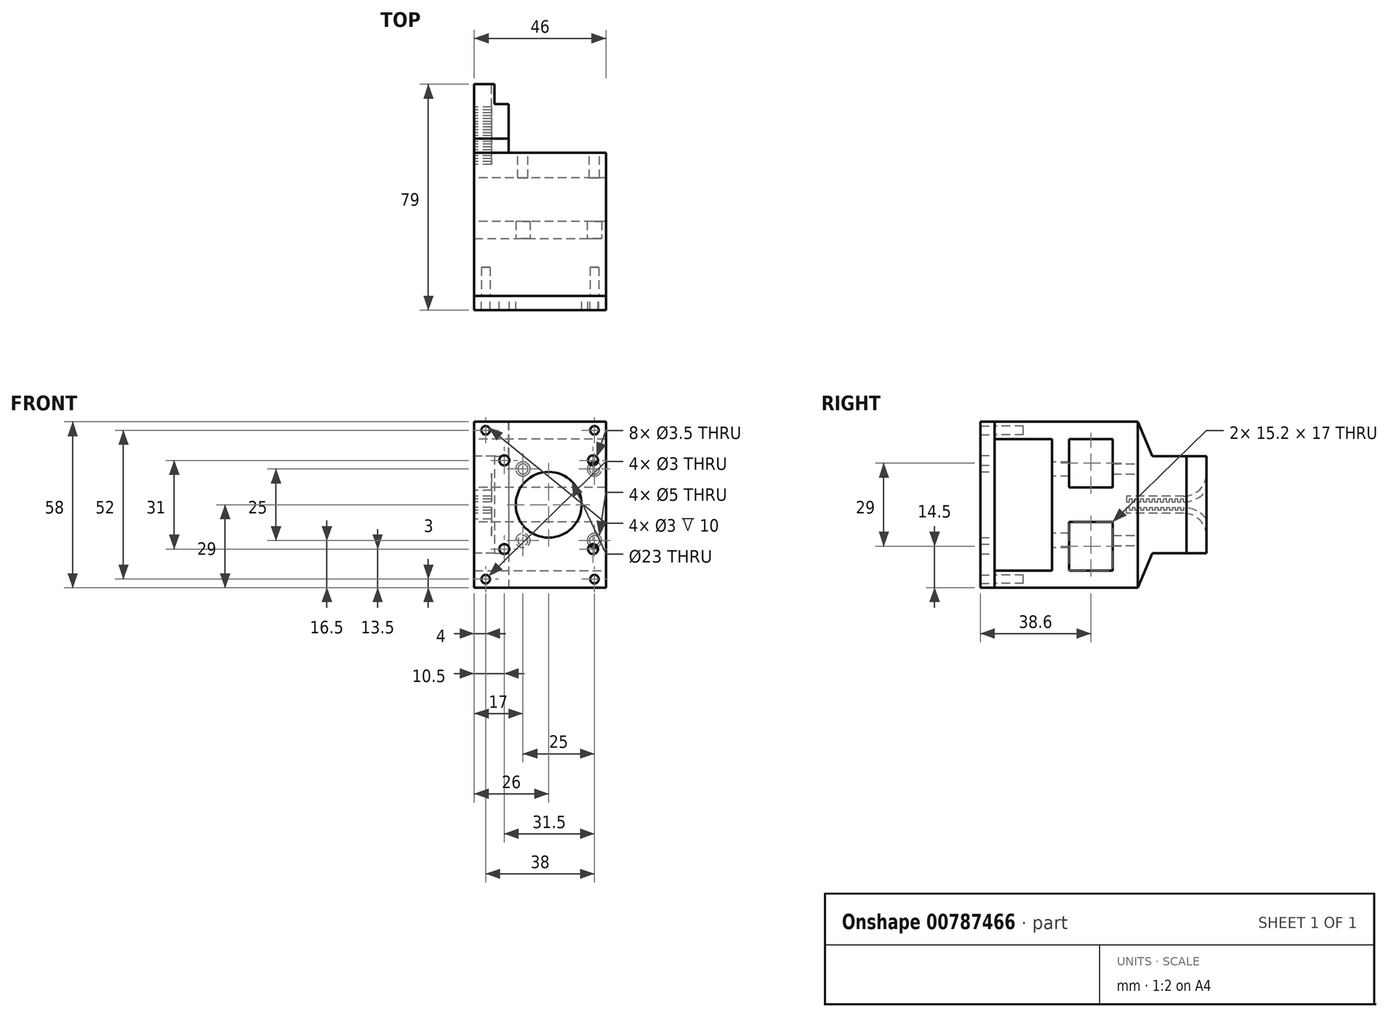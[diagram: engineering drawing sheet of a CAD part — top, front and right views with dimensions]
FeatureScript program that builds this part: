
annotation { "Feature Type Name" : "Feature", "Feature Type Description" : "" }
export const myFeature = defineFeature(function(context is Context, id is Id, definition is map)
    precondition{}
    {
        {
            var Q0;
            Q0=qCreatedBy(makeId("Front.planeOp"),FACE);
            var sketch = newSketch(context, id + "F0", { "sketchPlane" : qUnion([Q0])});
            skLineSegment(sketch, "E0.bottom", {"start": v(0, 0) * mm, "end": v(46, 0) * mm});
            skLineSegment(sketch, "E0.top", {"start": v(0, 58) * mm, "end": v(46, 58) * mm});
            skLineSegment(sketch, "E0.left", {"start": v(0, 0) * mm, "end": v(0, 58) * mm});
            skLineSegment(sketch, "E0.right", {"start": v(46, 0) * mm, "end": v(46, 58) * mm});
            skCircle(sketch, "E1", {"center": v(17, 16.5) * mm, "radius": 1.75 * mm});
            skCircle(sketch, "E2", {"center": v(42, 16.5) * mm, "radius": 1.75 * mm});
            skCircle(sketch, "E3", {"center": v(42, 41.5) * mm, "radius": 1.75 * mm});
            skCircle(sketch, "E4", {"center": v(17, 41.5) * mm, "radius": 1.75 * mm});
            skLineSegment(sketch, "E5", {"start": v(-7.47, 16.5) * mm, "end": v(45.4, 16.5) * mm, "construction": true});
            skLineSegment(sketch, "E6", {"start": v(-6.97, 41.5) * mm, "end": v(44.16, 41.5) * mm, "construction": true});
            skLineSegment(sketch, "E7", {"start": v(17, -1.28) * mm, "end": v(17, 38.84) * mm, "construction": true});
            skLineSegment(sketch, "E8", {"start": v(42, -1.84) * mm, "end": v(42, 37.95) * mm, "construction": true});
            skLineSegment(sketch, "E9", {"start": v(42, 37.95) * mm, "end": v(41.66, 37.95) * mm, "construction": true});
            skSolve(sketch);
        }
        {
            var Q0;
            Q0=makeQuery(id+"F0.imprint","IMPRINT",FACE,{"disambiguationData":[TD([[makeQuery(id+"F0.imprint","IMPRINT",EDGE,{"derivedFrom":sQuery(id+"F0.wireOp",EDGE,"E0.bottom")}),1.0]])]});
            extrude(context, id + "F1", {"entities" : qUnion([Q0]), "depth" : 30 * mm, "offsetDistance" : 25 * mm});
        }
        {
            var Q0;
            Q0=makeQuery(id+"Fh8Oho9HevaeckM_1.boolean.opBoolean","MERGE",FACE,{"derivedFrom":[makeQuery(id+"F5.boolean.opBoolean","MERGE",FACE,{"derivedFrom":[makeQuery(id+"F1.opExtrude","SWEPT_FACE",FACE,{"disambiguationData":[OSD([sQuery(id+"F0.wireOp",EDGE,"E0.left")])]}),makeQuery(id+"F5.opExtrude","SWEPT_FACE",FACE,{"disambiguationData":[OSD([sQuery(id+"F4.wireOp",EDGE,"E16.right")])]})]}),makeQuery(id+"Fh8Oho9HevaeckM_1.opExtrude","SWEPT_FACE",FACE,{"disambiguationData":[OSD([sQuery(id+"FOvHqaYxA9nbsMf_1.wireOp",EDGE,"oteaciAY-sE7d-qbvy-cTgZ-kNNArxGtZx8z.left")])]})]});
            var sketch = newSketch(context, id + "F2", { "sketchPlane" : qUnion([Q0])});
            skLineSegment(sketch, "E10.bottom", {"start": v(8.8, 6) * mm, "end": v(24, 6) * mm});
            skLineSegment(sketch, "E10.top", {"start": v(8.8, 23) * mm, "end": v(24, 23) * mm});
            skLineSegment(sketch, "E10.left", {"start": v(8.8, 6) * mm, "end": v(8.8, 23) * mm});
            skLineSegment(sketch, "E10.right", {"start": v(24, 6) * mm, "end": v(24, 23) * mm});
            skPoint(sketch, "E10.middle", {"position": v(16.4, 14.5) * mm});
            skLineSegment(sketch, "E11", {"start": v(30, 29) * mm, "end": v(0, 29) * mm, "construction": true});
            skLineSegment(sketch, "E12.MirrorCS", {"start": v(8.8, 35) * mm, "end": v(24, 35) * mm});
            skLineSegment(sketch, "E13.MirrorCS", {"start": v(24, 52) * mm, "end": v(24, 35) * mm});
            skLineSegment(sketch, "E14.MirrorCS", {"start": v(8.8, 52) * mm, "end": v(24, 52) * mm});
            skLineSegment(sketch, "E15.MirrorCS", {"start": v(8.8, 52) * mm, "end": v(8.8, 35) * mm});
            skSolve(sketch);
        }
        {
            var Q0;
            Q0=qSketchRegion(id+"F2",true);
            extrude(context, id + "F3", {"entities" : qUnion([Q0]), "operationType" : NewBodyOperationType.REMOVE, "endBound" : BoundingType.THROUGH_ALL, "oppositeDirection" : true, "depth" : 25 * mm, "offsetDistance" : 25 * mm});
        }
        {
            var Q0;
            {var subQ0=sQuery(id+"F0.wireOp",EDGE,"E1");var subQ1=sQuery(id+"F0.wireOp",EDGE,"E0.right");var subQ2=sQuery(id+"F0.wireOp",EDGE,"E0.left");var subQ3=sQuery(id+"F0.wireOp",EDGE,"E0.top");var subQ4=sQuery(id+"F0.wireOp",EDGE,"E2");var subQ5=sQuery(id+"F0.wireOp",EDGE,"E3");var subQ6=sQuery(id+"F0.wireOp",EDGE,"E4");Q0=makeQuery(id+"FCBNdEiGlgR24Ja_1.boolean.opBoolean","SPLIT",FACE,{"disambiguationData":[TD([makeQuery(id+"F1.opExtrude","SWEPT_FACE",FACE,{"disambiguationData":[OSD([subQ3])]})])],"derivedFrom":makeQuery(id+"F1.opExtrude","CAP_FACE",FACE,{"disambiguationData":[OSD([sQuery(id+"F0.wireOp",EDGE,"E0.bottom"),subQ3,subQ2,subQ1,subQ0,subQ4,subQ5,subQ6])],"isStart":false})});}
            var sketch = newSketch(context, id + "F4", { "sketchPlane" : qUnion([Q0])});
            skLineSegment(sketch, "E16.bottom", {"start": v(46, 58) * mm, "end": v(0, 58) * mm});
            skLineSegment(sketch, "E16.top", {"start": v(46, 52) * mm, "end": v(0, 52) * mm});
            skLineSegment(sketch, "E16.left", {"start": v(46, 52) * mm, "end": v(46, 58) * mm});
            skLineSegment(sketch, "E16.right", {"start": v(0, 52) * mm, "end": v(0, 58) * mm});
            skLineSegment(sketch, "E17.bottom", {"start": v(0, 0) * mm, "end": v(46, 0) * mm});
            skLineSegment(sketch, "E17.top", {"start": v(0, 6) * mm, "end": v(46, 6) * mm});
            skLineSegment(sketch, "E17.left", {"start": v(0, 0) * mm, "end": v(0, 6) * mm});
            skLineSegment(sketch, "E17.right", {"start": v(46, 0) * mm, "end": v(46, 6) * mm});
            skSolve(sketch);
        }
        {
            var Q0;
            Q0 = qSketchRegion(id + "F4", true);
            extrude(context, id + "F5", {"entities" : qUnion([Q0]), "operationType" : NewBodyOperationType.ADD, "depth" : 20 * mm, "offsetDistance" : 25 * mm});
        }
        {
            var Q0;
            Q0=makeQuery(id+"F5.opExtrude","CAP_FACE",FACE,{"disambiguationData":[OSD([sQuery(id+"F4.wireOp",EDGE,"E16.bottom"),sQuery(id+"F4.wireOp",EDGE,"E16.top"),sQuery(id+"F4.wireOp",EDGE,"E16.left"),sQuery(id+"F4.wireOp",EDGE,"E16.right")])],"isStart":false});
            var sketch = newSketch(context, id + "F6", { "sketchPlane" : qUnion([Q0])});
            skLineSegment(sketch, "E18", {"start": v(26, 81.43) * mm, "end": v(26, 7.23) * mm, "construction": true});
            skPoint(sketch, "E18.startSnap0", {"position": v(26, 65.8) * mm});
            skLineSegment(sketch, "E19", {"start": v(-30.8, 29) * mm, "end": v(63.7, 29) * mm, "construction": true});
            skCircle(sketch, "E20", {"center": v(26, 29) * mm, "radius": 11.5 * mm});
            skCircle(sketch, "E21", {"center": v(10.5, 44.5) * mm, "radius": 1.75 * mm});
            skCircle(sketch, "E22.MirrorC", {"center": v(41.5, 44.5) * mm, "radius": 1.75 * mm});
            skCircle(sketch, "E23.MirrorC", {"center": v(10.5, 13.5) * mm, "radius": 1.75 * mm});
            skCircle(sketch, "E24.MirrorC", {"center": v(41.5, 13.5) * mm, "radius": 1.75 * mm});
            skLineSegment(sketch, "E25.bottom", {"start": v(46, 58) * mm, "end": v(0, 58) * mm});
            skLineSegment(sketch, "E25.top", {"start": v(46, 52) * mm, "end": v(0, 52) * mm});
            skLineSegment(sketch, "E25.left", {"start": v(46, 58) * mm, "end": v(46, 52) * mm});
            skLineSegment(sketch, "E25.right", {"start": v(0, 58) * mm, "end": v(0, 52) * mm});
            skLineSegment(sketch, "E26.bottom", {"start": v(0, 0) * mm, "end": v(46, 0) * mm});
            skLineSegment(sketch, "E26.top", {"start": v(0, 4.54) * mm, "end": v(46, 4.54) * mm});
            skLineSegment(sketch, "E26.left", {"start": v(0, 0) * mm, "end": v(0, 4.54) * mm});
            skLineSegment(sketch, "E26.right", {"start": v(46, 0) * mm, "end": v(46, 4.54) * mm});
            skLineSegment(sketch, "E27", {"start": v(46, 4.54) * mm, "end": v(46, 52) * mm});
            skLineSegment(sketch, "E28", {"start": v(0, 4.54) * mm, "end": v(0, 52) * mm});
            skSolve(sketch);
        }
        {
            var Q0;
            Q0 = qSketchRegion(id + "F6", true);
            extrude(context, id + "F7", {"entities" : qUnion([Q0]), "depth" : 5 * mm, "offsetDistance" : 25 * mm});
        }
        {
            var Q0;
            Q0=makeQuery(id+"F1.opExtrude","CAP_FACE",FACE,{"disambiguationData":[OSD([sQuery(id+"F0.wireOp",EDGE,"E0.bottom"),sQuery(id+"F0.wireOp",EDGE,"E0.top"),sQuery(id+"F0.wireOp",EDGE,"E0.left"),sQuery(id+"F0.wireOp",EDGE,"E0.right"),sQuery(id+"F0.wireOp",EDGE,"E1"),sQuery(id+"F0.wireOp",EDGE,"E2"),sQuery(id+"F0.wireOp",EDGE,"E3"),sQuery(id+"F0.wireOp",EDGE,"E4")])],"isStart":false});
            var sketch = newSketch(context, id + "F8", { "sketchPlane" : qUnion([Q0])});
            skCircle(sketch, "E29", {"center": v(17, 41.5) * mm, "radius": 2.5 * mm});
            skCircle(sketch, "E30", {"center": v(17, 16.5) * mm, "radius": 2.5 * mm});
            skCircle(sketch, "E31", {"center": v(42, 41.5) * mm, "radius": 2.5 * mm});
            skCircle(sketch, "E32", {"center": v(42, 16.5) * mm, "radius": 2.5 * mm});
            skSolve(sketch);
        }
        {
            var Q0;
            Q0 = qSketchRegion(id + "F8", true);
            extrude(context, id + "F9", {"entities" : qUnion([Q0]), "operationType" : NewBodyOperationType.REMOVE, "oppositeDirection" : true, "depth" : 10 * mm, "offsetDistance" : 25 * mm});
        }
        {
            var Q0;
            Q0=makeQuery(id+"F6.imprint","IMPRINT",FACE,{"disambiguationData":[TD([[makeQuery(id+"F6.imprint","IMPRINT",EDGE,{"derivedFrom":sQuery(id+"F6.wireOp",EDGE,"E26.bottom")}),1.0]])]});
            var sketch = newSketch(context, id + "F10", { "sketchPlane" : qUnion([Q0])});
            skLineSegment(sketch, "E33", {"start": v(41.02, 3) * mm, "end": v(0, 3) * mm, "construction": true});
            skCircle(sketch, "E34", {"center": v(42, 3) * mm, "radius": 1.5 * mm});
            skCircle(sketch, "E35", {"center": v(4, 3) * mm, "radius": 1.5 * mm});
            skLineSegment(sketch, "E36", {"start": v(46, 55) * mm, "end": v(0, 55) * mm, "construction": true});
            skCircle(sketch, "E37", {"center": v(42, 55) * mm, "radius": 1.5 * mm});
            skCircle(sketch, "E38", {"center": v(4, 55) * mm, "radius": 1.5 * mm});
            skSolve(sketch);
        }
        {
            var Q0;
            Q0 = qSketchRegion(id + "F10", true);
            extrude(context, id + "F11", {"entities" : qUnion([Q0]), "operationType" : NewBodyOperationType.REMOVE, "oppositeDirection" : true, "depth" : 10 * mm, "offsetDistance" : 25 * mm});
        }
        {
            var Q0;
            Q0 = qSketchRegion(id + "F10", true);
            extrude(context, id + "F12", {"entities" : qUnion([Q0]), "operationType" : NewBodyOperationType.REMOVE, "endBound" : BoundingType.THROUGH_ALL, "depth" : 25 * mm, "offsetDistance" : 25 * mm});
        }
        {
            var Q0;
            Q0=makeQuery(id+"F1.opExtrude","CAP_FACE",FACE,{"disambiguationData":[OSD([sQuery(id+"F0.wireOp",EDGE,"E0.bottom"),sQuery(id+"F0.wireOp",EDGE,"E0.top"),sQuery(id+"F0.wireOp",EDGE,"E0.left"),sQuery(id+"F0.wireOp",EDGE,"E0.right"),sQuery(id+"F0.wireOp",EDGE,"E1"),sQuery(id+"F0.wireOp",EDGE,"E2"),sQuery(id+"F0.wireOp",EDGE,"E3"),sQuery(id+"F0.wireOp",EDGE,"E4")])],"isStart":true});
            var sketch = newSketch(context, id + "F13", { "sketchPlane" : qUnion([Q0])});
            skLineSegment(sketch, "E39.bottom", {"start": v(0, 58) * mm, "end": v(-12, 58) * mm});
            skLineSegment(sketch, "E39.top", {"start": v(0, 0) * mm, "end": v(-12, 0) * mm});
            skLineSegment(sketch, "E39.left", {"start": v(0, 58) * mm, "end": v(0, 0) * mm});
            skLineSegment(sketch, "E39.right", {"start": v(-12, 58) * mm, "end": v(-12, 0) * mm});
            skSolve(sketch);
        }
        {
            var Q0;
            Q0=makeQuery(id+"F13.imprint","IMPRINT",FACE,{"disambiguationData":[TD([[makeQuery(id+"F13.imprint","IMPRINT",EDGE,{"derivedFrom":sQuery(id+"F13.wireOp",EDGE,"E39.bottom")}),1.0]])]});
            extrude(context, id + "F14", {"entities" : qUnion([Q0]), "operationType" : NewBodyOperationType.ADD, "depth" : 24 * mm, "offsetDistance" : 25 * mm});
        }
        {
            var Q0;
            Q0=makeQuery(id+"F14.boolean.opBoolean","MERGE",FACE,{"derivedFrom":[makeQuery(id+"F5.boolean.opBoolean","MERGE",FACE,{"derivedFrom":[makeQuery(id+"F1.opExtrude","SWEPT_FACE",FACE,{"disambiguationData":[OSD([sQuery(id+"F0.wireOp",EDGE,"E0.left")])]}),makeQuery(id+"F5.opExtrude","SWEPT_FACE",FACE,{"disambiguationData":[OSD([sQuery(id+"F4.wireOp",EDGE,"E16.right")])]}),makeQuery(id+"F5.opExtrude","SWEPT_FACE",FACE,{"disambiguationData":[OSD([sQuery(id+"F4.wireOp",EDGE,"E17.left")])]})]}),makeQuery(id+"F14.opExtrude","SWEPT_FACE",FACE,{"disambiguationData":[OSD([sQuery(id+"F13.wireOp",EDGE,"E39.left")])]})]});
            var sketch = newSketch(context, id + "F15", { "sketchPlane" : qUnion([Q0])});
            skLineSegment(sketch, "E40", {"start": v(-24, 29) * mm, "end": v(30, 29) * mm, "construction": true});
            skLineSegment(sketch, "E41", {"start": v(30, 29) * mm, "end": v(29.17, 29.8) * mm, "construction": true});
            skArc(sketch, "E42", {"start": v(-24, 40) * mm, "mid": v(-21.66, 34.34) * mm, "end": v(-16, 32) * mm});
            skLineSegment(sketch, "E43", {"start": v(-16, 32) * mm, "end": v(4, 32) * mm});
            skLineSegment(sketch, "E44", {"start": v(4, 32) * mm, "end": v(4, 30) * mm});
            skLineSegment(sketch, "E45", {"start": v(4, 30) * mm, "end": v(3, 30) * mm});
            skArc(sketch, "E46", {"start": v(-24, 34) * mm, "mid": v(-20.47, 31.06) * mm, "end": v(-16, 30) * mm});
            skPoint(sketch, "E47.start.orphan", {"position": v(0, 58) * mm});
            skLineSegment(sketch, "E48", {"start": v(-24, 34) * mm, "end": v(-24, 40) * mm});
            skLineSegment(sketch, "E49", {"start": v(-16, 40) * mm, "end": v(-16, 24.86) * mm, "construction": true});
            skLineSegment(sketch, "E50.top", {"start": v(2, 31) * mm, "end": v(3, 31) * mm});
            skLineSegment(sketch, "E50.left", {"start": v(2, 30) * mm, "end": v(2, 31) * mm});
            skLineSegment(sketch, "E50.right", {"start": v(3, 30) * mm, "end": v(3, 31) * mm});
            skLineSegment(sketch, "E51.1.0.0", {"start": v(0, 30) * mm, "end": v(0, 31) * mm});
            skLineSegment(sketch, "E51.1.0.1", {"start": v(0, 31) * mm, "end": v(1, 31) * mm});
            skLineSegment(sketch, "E51.1.0.2", {"start": v(2, 30) * mm, "end": v(1, 30) * mm});
            skLineSegment(sketch, "E51.1.0.3", {"start": v(1, 30) * mm, "end": v(1, 31) * mm});
            skLineSegment(sketch, "E51.2.0.0", {"start": v(-2, 30) * mm, "end": v(-2, 31) * mm});
            skLineSegment(sketch, "E51.2.0.1", {"start": v(-2, 31) * mm, "end": v(-1, 31) * mm});
            skLineSegment(sketch, "E51.2.0.2", {"start": v(0, 30) * mm, "end": v(-1, 30) * mm});
            skLineSegment(sketch, "E51.2.0.3", {"start": v(-1, 30) * mm, "end": v(-1, 31) * mm});
            skLineSegment(sketch, "E51.3.0.0", {"start": v(-4, 30) * mm, "end": v(-4, 31) * mm});
            skLineSegment(sketch, "E51.3.0.1", {"start": v(-4, 31) * mm, "end": v(-3, 31) * mm});
            skLineSegment(sketch, "E51.3.0.2", {"start": v(-2, 30) * mm, "end": v(-3, 30) * mm});
            skLineSegment(sketch, "E51.3.0.3", {"start": v(-3, 30) * mm, "end": v(-3, 31) * mm});
            skLineSegment(sketch, "E51.4.0.0", {"start": v(-6, 30) * mm, "end": v(-6, 31) * mm});
            skLineSegment(sketch, "E51.4.0.1", {"start": v(-6, 31) * mm, "end": v(-5, 31) * mm});
            skLineSegment(sketch, "E51.4.0.2", {"start": v(-4, 30) * mm, "end": v(-5, 30) * mm});
            skLineSegment(sketch, "E51.4.0.3", {"start": v(-5, 30) * mm, "end": v(-5, 31) * mm});
            skLineSegment(sketch, "E51.5.0.0", {"start": v(-8, 30) * mm, "end": v(-8, 31) * mm});
            skLineSegment(sketch, "E51.5.0.1", {"start": v(-8, 31) * mm, "end": v(-7, 31) * mm});
            skLineSegment(sketch, "E51.5.0.2", {"start": v(-6, 30) * mm, "end": v(-7, 30) * mm});
            skLineSegment(sketch, "E51.5.0.3", {"start": v(-7, 30) * mm, "end": v(-7, 31) * mm});
            skLineSegment(sketch, "E51.6.0.0", {"start": v(-10, 30) * mm, "end": v(-10, 31) * mm});
            skLineSegment(sketch, "E51.6.0.1", {"start": v(-10, 31) * mm, "end": v(-9, 31) * mm});
            skLineSegment(sketch, "E51.6.0.2", {"start": v(-8, 30) * mm, "end": v(-9, 30) * mm});
            skLineSegment(sketch, "E51.6.0.3", {"start": v(-9, 30) * mm, "end": v(-9, 31) * mm});
            skLineSegment(sketch, "E51.7.0.0", {"start": v(-12, 30) * mm, "end": v(-12, 31) * mm});
            skLineSegment(sketch, "E51.7.0.1", {"start": v(-12, 31) * mm, "end": v(-11, 31) * mm});
            skLineSegment(sketch, "E51.7.0.2", {"start": v(-10, 30) * mm, "end": v(-11, 30) * mm});
            skLineSegment(sketch, "E51.7.0.3", {"start": v(-11, 30) * mm, "end": v(-11, 31) * mm});
            skLineSegment(sketch, "E51.8.0.0", {"start": v(-14, 30) * mm, "end": v(-14, 31) * mm});
            skLineSegment(sketch, "E51.8.0.1", {"start": v(-14, 31) * mm, "end": v(-13, 31) * mm});
            skLineSegment(sketch, "E51.8.0.2", {"start": v(-12, 30) * mm, "end": v(-13, 30) * mm});
            skLineSegment(sketch, "E51.8.0.3", {"start": v(-13, 30) * mm, "end": v(-13, 31) * mm});
            skLineSegment(sketch, "E51.9.0.0", {"start": v(-16, 30) * mm, "end": v(-16, 31) * mm});
            skLineSegment(sketch, "E51.9.0.1", {"start": v(-16, 31) * mm, "end": v(-15, 31) * mm});
            skLineSegment(sketch, "E51.9.0.2", {"start": v(-14, 30) * mm, "end": v(-15, 30) * mm});
            skLineSegment(sketch, "E51.9.0.3", {"start": v(-15, 30) * mm, "end": v(-15, 31) * mm});
            skLineSegment(sketch, "E51.direction1", {"start": v(2, 30) * mm, "end": v(0, 30) * mm, "construction": true});
            skLineSegment(sketch, "E52.MirrorCS", {"start": v(-3, 28) * mm, "end": v(-3, 27) * mm});
            skLineSegment(sketch, "E53.MirrorCS", {"start": v(-11, 28) * mm, "end": v(-11, 27) * mm});
            skLineSegment(sketch, "E54.MirrorCS", {"start": v(-6, 27) * mm, "end": v(-5, 27) * mm});
            skLineSegment(sketch, "E55.MirrorCS", {"start": v(-14, 27) * mm, "end": v(-13, 27) * mm});
            skLineSegment(sketch, "E56.MirrorCS", {"start": v(-5, 28) * mm, "end": v(-5, 27) * mm});
            skLineSegment(sketch, "E57.MirrorCS", {"start": v(-13, 28) * mm, "end": v(-13, 27) * mm});
            skLineSegment(sketch, "E58.MirrorCS", {"start": v(0, 28) * mm, "end": v(0, 27) * mm});
            skLineSegment(sketch, "E59.MirrorCS", {"start": v(3, 28) * mm, "end": v(3, 27) * mm});
            skLineSegment(sketch, "E60.MirrorCS", {"start": v(2, 28) * mm, "end": v(2, 27) * mm});
            skLineSegment(sketch, "E61.MirrorCS", {"start": v(2, 27) * mm, "end": v(3, 27) * mm});
            skLineSegment(sketch, "E62.MirrorCS", {"start": v(4, 28) * mm, "end": v(3, 28) * mm});
            skLineSegment(sketch, "E63.MirrorCS", {"start": v(-10, 28) * mm, "end": v(-10, 27) * mm});
            skLineSegment(sketch, "E64.MirrorCS", {"start": v(2, 28) * mm, "end": v(0, 28) * mm, "construction": true});
            skLineSegment(sketch, "E65.MirrorCS", {"start": v(-2, 28) * mm, "end": v(-2, 27) * mm});
            skLineSegment(sketch, "E66.MirrorCS", {"start": v(2, 28) * mm, "end": v(1, 28) * mm});
            skLineSegment(sketch, "E67.MirrorCS", {"start": v(-8, 28) * mm, "end": v(-9, 28) * mm});
            skLineSegment(sketch, "E68.MirrorCS", {"start": v(0, 27) * mm, "end": v(1, 27) * mm});
            skLineSegment(sketch, "E69.MirrorCS", {"start": v(0, 28) * mm, "end": v(-1, 28) * mm});
            skLineSegment(sketch, "E70.MirrorCS", {"start": v(1, 28) * mm, "end": v(1, 27) * mm});
            skLineSegment(sketch, "E71.MirrorCS", {"start": v(-12, 28) * mm, "end": v(-12, 27) * mm});
            skLineSegment(sketch, "E72.MirrorCS", {"start": v(-8, 27) * mm, "end": v(-7, 27) * mm});
            skLineSegment(sketch, "E73.MirrorCS", {"start": v(-16, 27) * mm, "end": v(-15, 27) * mm});
            skLineSegment(sketch, "E74.MirrorCS", {"start": v(-4, 28) * mm, "end": v(-4, 27) * mm});
            skLineSegment(sketch, "E75.MirrorCS", {"start": v(-2, 28) * mm, "end": v(-3, 28) * mm});
            skLineSegment(sketch, "E76.MirrorCS", {"start": v(-10, 28) * mm, "end": v(-11, 28) * mm});
            skLineSegment(sketch, "E77.MirrorCS", {"start": v(-6, 28) * mm, "end": v(-6, 27) * mm});
            skLineSegment(sketch, "E78.MirrorCS", {"start": v(-14, 28) * mm, "end": v(-14, 27) * mm});
            skLineSegment(sketch, "E79.MirrorCS", {"start": v(-4, 28) * mm, "end": v(-5, 28) * mm});
            skLineSegment(sketch, "E80.MirrorCS", {"start": v(-12, 28) * mm, "end": v(-13, 28) * mm});
            skLineSegment(sketch, "E81.MirrorCS", {"start": v(-8, 28) * mm, "end": v(-8, 27) * mm});
            skLineSegment(sketch, "E82.MirrorCS", {"start": v(-16, 28) * mm, "end": v(-16, 27) * mm});
            skLineSegment(sketch, "E83.MirrorCS", {"start": v(-10, 27) * mm, "end": v(-9, 27) * mm});
            skLineSegment(sketch, "E84.MirrorCS", {"start": v(-2, 27) * mm, "end": v(-1, 27) * mm});
            skLineSegment(sketch, "E85.MirrorCS", {"start": v(-7, 28) * mm, "end": v(-7, 27) * mm});
            skLineSegment(sketch, "E86.MirrorCS", {"start": v(-9, 28) * mm, "end": v(-9, 27) * mm});
            skLineSegment(sketch, "E87.MirrorCS", {"start": v(-15, 28) * mm, "end": v(-15, 27) * mm});
            skLineSegment(sketch, "E88.MirrorCS", {"start": v(-1, 28) * mm, "end": v(-1, 27) * mm});
            skLineSegment(sketch, "E89.MirrorCS", {"start": v(-12, 27) * mm, "end": v(-11, 27) * mm});
            skLineSegment(sketch, "E90.MirrorCS", {"start": v(-6, 28) * mm, "end": v(-7, 28) * mm});
            skLineSegment(sketch, "E91.MirrorCS", {"start": v(-14, 28) * mm, "end": v(-15, 28) * mm});
            skLineSegment(sketch, "E92.MirrorCS", {"start": v(-4, 27) * mm, "end": v(-3, 27) * mm});
            skLineSegment(sketch, "E93.MirrorCS", {"start": v(-16, 18) * mm, "end": v(-16, 33.14) * mm, "construction": true});
            skLineSegment(sketch, "E94.MirrorCS", {"start": v(-24, 24) * mm, "end": v(-24, 18) * mm});
            skArc(sketch, "E95.MirrorCS", {"start": v(-24, 24) * mm, "mid": v(-20.47, 26.94) * mm, "end": v(-16, 28) * mm});
            skLineSegment(sketch, "E96.MirrorCS", {"start": v(4, 26) * mm, "end": v(4, 28) * mm});
            skLineSegment(sketch, "E97.MirrorCS", {"start": v(-16, 26) * mm, "end": v(4, 26) * mm});
            skArc(sketch, "E98.MirrorCS", {"start": v(-24, 18) * mm, "mid": v(-21.66, 23.66) * mm, "end": v(-16, 26) * mm});
            skSolve(sketch);
        }
        {
            var Q0;
            Q0 = qSketchRegion(id + "F15", true);
            extrude(context, id + "F16", {"entities" : qUnion([Q0]), "operationType" : NewBodyOperationType.REMOVE, "oppositeDirection" : true, "depth" : 6 * mm, "offsetDistance" : 25 * mm});
        }
        {
            var Q0;
            Q0=makeQuery(id+"F14.boolean.opBoolean","MERGE",FACE,{"derivedFrom":[makeQuery(id+"F5.boolean.opBoolean","MERGE",FACE,{"derivedFrom":[makeQuery(id+"F1.opExtrude","SWEPT_FACE",FACE,{"disambiguationData":[OSD([sQuery(id+"F0.wireOp",EDGE,"E0.left")])]}),makeQuery(id+"F5.opExtrude","SWEPT_FACE",FACE,{"disambiguationData":[OSD([sQuery(id+"F4.wireOp",EDGE,"E16.right")])]}),makeQuery(id+"F5.opExtrude","SWEPT_FACE",FACE,{"disambiguationData":[OSD([sQuery(id+"F4.wireOp",EDGE,"E17.left")])]})]}),makeQuery(id+"F14.opExtrude","SWEPT_FACE",FACE,{"disambiguationData":[OSD([sQuery(id+"F13.wireOp",EDGE,"E39.left")])]})]});
            var sketch = newSketch(context, id + "F17", { "sketchPlane" : qUnion([Q0])});
            skLineSegment(sketch, "E99", {"start": v(-24, 46) * mm, "end": v(-5, 46) * mm});
            skLineSegment(sketch, "E100", {"start": v(-5, 46) * mm, "end": v(0, 58) * mm});
            skLineSegment(sketch, "E101", {"start": v(0, 58) * mm, "end": v(-24, 58) * mm});
            skLineSegment(sketch, "E102", {"start": v(-24, 58) * mm, "end": v(-24, 46) * mm});
            skLineSegment(sketch, "E103", {"start": v(-24, 29) * mm, "end": v(30, 29) * mm, "construction": true});
            skLineSegment(sketch, "E104", {"start": v(30, 29) * mm, "end": v(30.92, 29) * mm, "construction": true});
            skLineSegment(sketch, "E105.MirrorCS", {"start": v(-24, 0) * mm, "end": v(-24, 12) * mm});
            skLineSegment(sketch, "E106.MirrorCS", {"start": v(-24, 12) * mm, "end": v(-5, 12) * mm});
            skLineSegment(sketch, "E107.MirrorCS", {"start": v(0, 0) * mm, "end": v(-24, 0) * mm});
            skLineSegment(sketch, "E108.MirrorCS", {"start": v(-5, 12) * mm, "end": v(0, 0) * mm});
            skSolve(sketch);
        }
        {
            var Q0;
            Q0 = qSketchRegion(id + "F17", true);
            extrude(context, id + "F18", {"entities" : qUnion([Q0]), "operationType" : NewBodyOperationType.REMOVE, "endBound" : BoundingType.THROUGH_ALL, "oppositeDirection" : true, "depth" : 25 * mm, "offsetDistance" : 25 * mm});
        }
        {
            var Q0;
            Q0=makeQuery(id+"F14.opExtrude","SWEPT_FACE",FACE,{"disambiguationData":[OSD([sQuery(id+"F13.wireOp",EDGE,"E39.right")])]});
            var sketch = newSketch(context, id + "F19", { "sketchPlane" : qUnion([Q0])});
            skLineSegment(sketch, "E109.bottom", {"start": v(24, 46) * mm, "end": v(17, 46) * mm});
            skLineSegment(sketch, "E109.top", {"start": v(24, 12) * mm, "end": v(17, 12) * mm});
            skLineSegment(sketch, "E109.left", {"start": v(24, 46) * mm, "end": v(24, 12) * mm});
            skLineSegment(sketch, "E109.right", {"start": v(17, 46) * mm, "end": v(17, 12) * mm});
            skSolve(sketch);
        }
        {
            var Q0;
            Q0=makeQuery(id+"F19.imprint","IMPRINT",FACE,{"disambiguationData":[TD([[makeQuery(id+"F19.imprint","IMPRINT",EDGE,{"derivedFrom":sQuery(id+"F19.wireOp",EDGE,"E109.bottom")}),1.0]])]});
            extrude(context, id + "F20", {"entities" : qUnion([Q0]), "operationType" : NewBodyOperationType.REMOVE, "oppositeDirection" : true, "depth" : 5 * mm, "offsetDistance" : 25 * mm});
        }
    });
